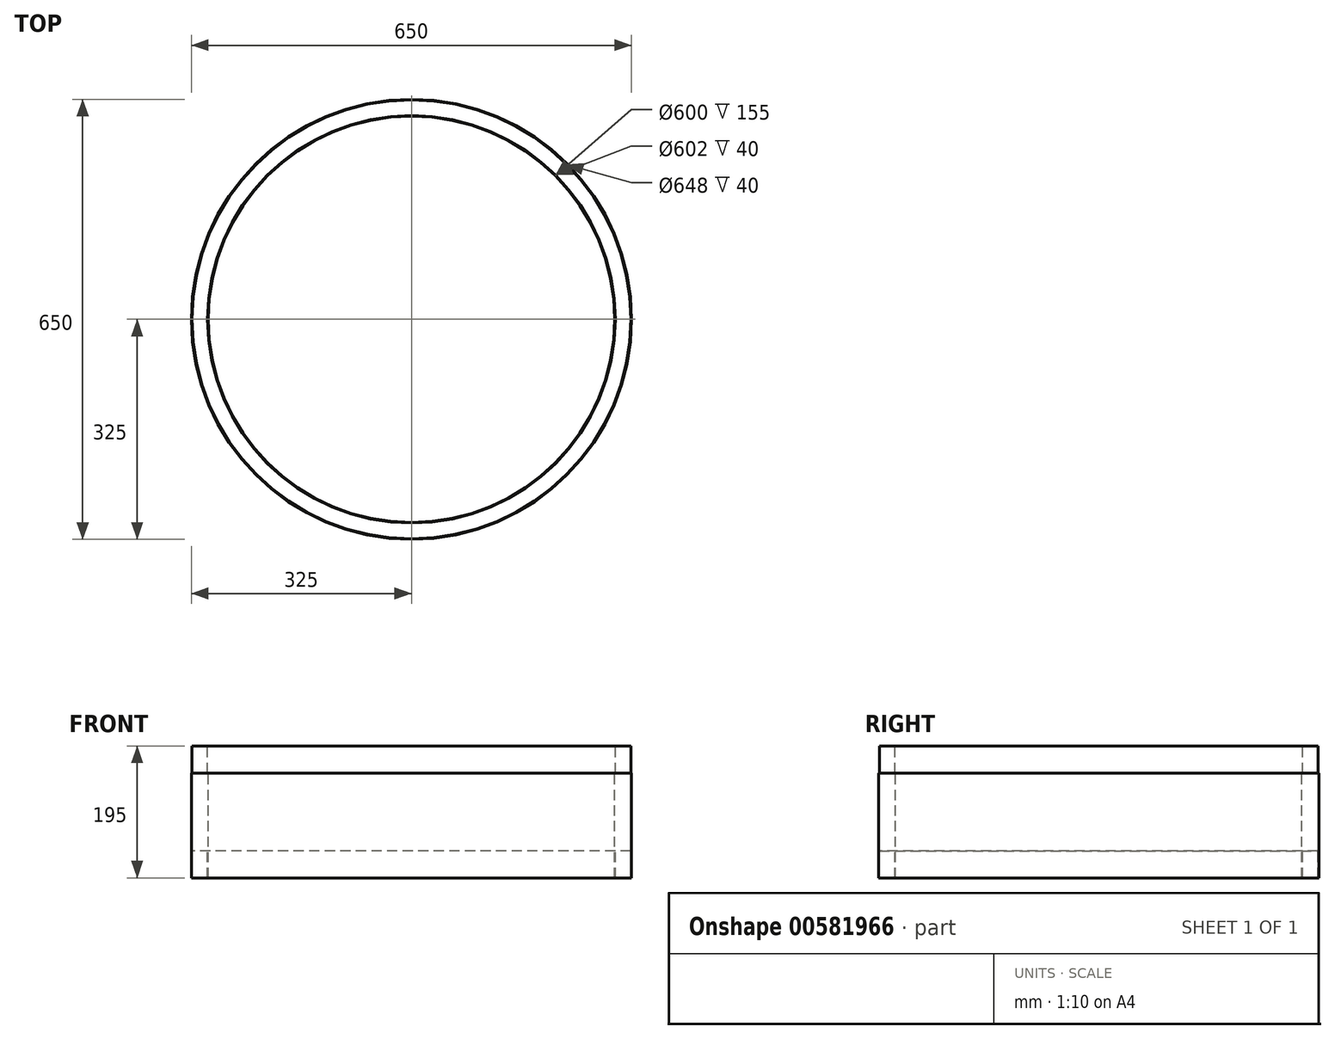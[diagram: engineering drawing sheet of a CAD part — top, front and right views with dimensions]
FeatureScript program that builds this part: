
annotation { "Feature Type Name" : "Feature", "Feature Type Description" : "" }
export const myFeature = defineFeature(function(context is Context, id is Id, definition is map)
    precondition{}
    {
        {
            var Q0;
            Q0=qCreatedBy(makeId("Front.planeOp"),FACE);
            var sketch = newSketch(context, id + "F0", { "sketchPlane" : qUnion([Q0])});
            skLineSegment(sketch, "E0", {"start": v(0, 345.75) * mm, "end": v(0, -558.03) * mm, "construction": true});
            skLineSegment(sketch, "E1", {"start": v(-300, -518.84) * mm, "end": v(-300, -363.84) * mm});
            skLineSegment(sketch, "E2", {"start": v(-300, -363.84) * mm, "end": v(-301, -363.84) * mm});
            skLineSegment(sketch, "E3", {"start": v(-301, -363.84) * mm, "end": v(-301, -323.84) * mm});
            skLineSegment(sketch, "E4", {"start": v(-301, -323.84) * mm, "end": v(-324, -323.84) * mm});
            skLineSegment(sketch, "E5", {"start": v(-324, -323.84) * mm, "end": v(-324, -363.84) * mm});
            skLineSegment(sketch, "E6", {"start": v(-324, -363.84) * mm, "end": v(-325, -363.84) * mm});
            skLineSegment(sketch, "E7", {"start": v(-325, -363.84) * mm, "end": v(-325, -518.84) * mm});
            skLineSegment(sketch, "E8", {"start": v(-325, -518.84) * mm, "end": v(-324, -518.84) * mm});
            skLineSegment(sketch, "E9", {"start": v(-324, -518.84) * mm, "end": v(-324, -478.84) * mm});
            skLineSegment(sketch, "E10", {"start": v(-324, -478.84) * mm, "end": v(-301, -478.84) * mm});
            skLineSegment(sketch, "E11", {"start": v(-301, -478.84) * mm, "end": v(-301, -518.84) * mm});
            skLineSegment(sketch, "E12", {"start": v(-301, -518.84) * mm, "end": v(-300, -518.84) * mm});
            skSolve(sketch);
        }
        {
            var Q0;
            Q0=qSketchRegion(id+"F0",true);
            var Q1;
            Q1=sQuery(id+"F0.wireOp",EDGE,"E0");
            revolve(context, id + "F1", {"entities" : qUnion([Q0]), "axis" : qUnion([Q1]), "revolveType" : RevolveType.FULL});
        }
    });
